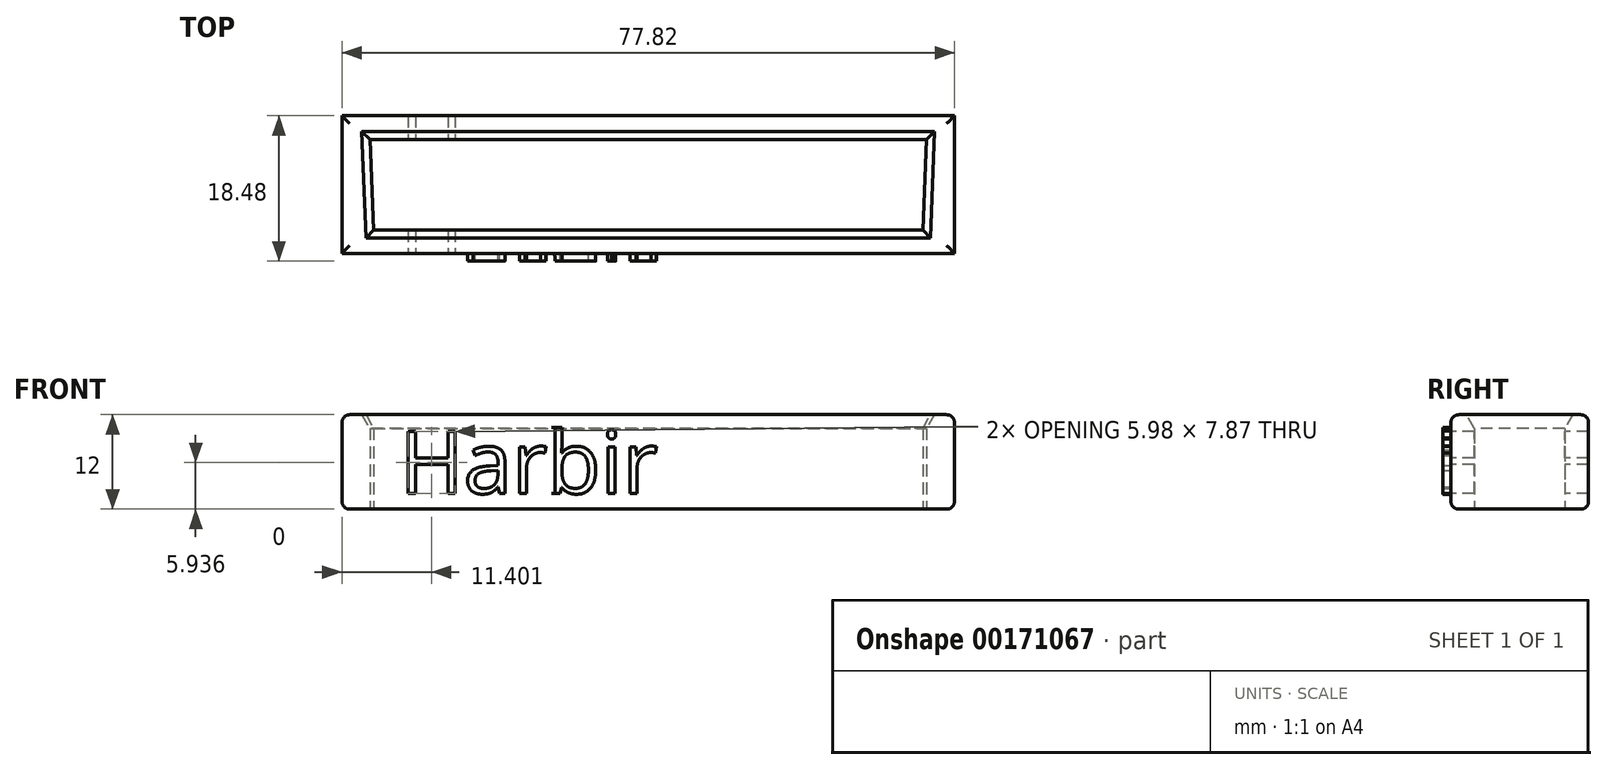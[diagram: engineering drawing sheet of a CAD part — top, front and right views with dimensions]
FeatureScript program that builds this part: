
annotation { "Feature Type Name" : "Feature", "Feature Type Description" : "" }
export const myFeature = defineFeature(function(context is Context, id is Id, definition is map)
    precondition{}
    {
        {
            var Q0;
            Q0=qCreatedBy(makeId("Top.planeOp"),FACE);
            var sketch = newSketch(context, id + "F0", { "sketchPlane" : qUnion([Q0])});
            skLineSegment(sketch, "E0.bottom", {"start": v(-32.53, 27.49) * mm, "end": v(38.17, 27.49) * mm});
            skLineSegment(sketch, "E0.top", {"start": v(-32.53, 16.09) * mm, "end": v(38.17, 16.09) * mm, "construction": true});
            skLineSegment(sketch, "E0.left", {"start": v(-32.53, 27.49) * mm, "end": v(-32.53, 16.09) * mm});
            skLineSegment(sketch, "E0.right", {"start": v(38.17, 27.49) * mm, "end": v(38.17, 16.09) * mm});
            skLineSegment(sketch, "E1", {"start": v(-32.08, 15.99) * mm, "end": v(37.72, 15.99) * mm});
            skLineSegment(sketch, "E2", {"start": v(2.82, 16.09) * mm, "end": v(2.82, 15.99) * mm, "construction": true});
            skLineSegment(sketch, "E3", {"start": v(-32.08, 15.99) * mm, "end": v(-32.53, 27.49) * mm});
            skLineSegment(sketch, "E4", {"start": v(37.72, 15.99) * mm, "end": v(38.17, 27.49) * mm});
            skLineSegment(sketch, "E5.bottom", {"start": v(-36.1, 30.5) * mm, "end": v(41.73, 30.5) * mm});
            skLineSegment(sketch, "E5.top", {"start": v(-36.1, 13.02) * mm, "end": v(41.73, 13.02) * mm});
            skLineSegment(sketch, "E5.left", {"start": v(-36.1, 30.5) * mm, "end": v(-36.1, 13.02) * mm});
            skLineSegment(sketch, "E5.right", {"start": v(41.73, 30.5) * mm, "end": v(41.73, 13.02) * mm});
            skLineSegment(sketch, "E6", {"start": v(2.82, 30.5) * mm, "end": v(2.82, 27.49) * mm, "construction": true});
            skSolve(sketch);
        }
        {
            var Q0;
            Q0=makeQuery(id+"F0.imprint","IMPRINT",FACE,{"disambiguationData":[TD([[makeQuery(id+"F0.imprint","IMPRINT",EDGE,{"derivedFrom":sQuery(id+"F0.wireOp",EDGE,"E0.bottom")}),1.0]])]});
            extrude(context, id + "F1", {"entities" : qUnion([Q0]), "depth" : 12 * mm});
        }
        {
            var Q0;
            Q0=makeQuery(id+"F1.opExtrude","CAP_EDGE",EDGE,{"disambiguationData":[OSD([sQuery(id+"F0.wireOp",EDGE,"E5.top")])],"isStart":false});
            var Q1;
            Q1=makeQuery(id+"F1.opExtrude","CAP_EDGE",EDGE,{"disambiguationData":[OSD([sQuery(id+"F0.wireOp",EDGE,"E5.left")])],"isStart":false});
            var Q2;
            Q2=makeQuery(id+"F1.opExtrude","CAP_EDGE",EDGE,{"disambiguationData":[OSD([sQuery(id+"F0.wireOp",EDGE,"E5.right")])],"isStart":false});
            var Q3;
            Q3=makeQuery(id+"F1.opExtrude","CAP_EDGE",EDGE,{"disambiguationData":[OSD([sQuery(id+"F0.wireOp",EDGE,"E5.bottom")])],"isStart":false});
            var Q4;
            Q4=makeQuery(id+"F1.opExtrude","CAP_EDGE",EDGE,{"disambiguationData":[OSD([sQuery(id+"F0.wireOp",EDGE,"E5.top")])],"isStart":true});
            var Q5;
            Q5=makeQuery(id+"F1.opExtrude","CAP_EDGE",EDGE,{"disambiguationData":[OSD([sQuery(id+"F0.wireOp",EDGE,"E5.right")])],"isStart":true});
            var Q6;
            Q6=makeQuery(id+"F1.opExtrude","CAP_EDGE",EDGE,{"disambiguationData":[OSD([sQuery(id+"F0.wireOp",EDGE,"E5.bottom")])],"isStart":true});
            var Q7;
            Q7=makeQuery(id+"F1.opExtrude","CAP_EDGE",EDGE,{"disambiguationData":[OSD([sQuery(id+"F0.wireOp",EDGE,"E5.left")])],"isStart":true});
            fillet(context, id + "F2", {"entities" : qUnion([Q0, Q1, Q2, Q3, Q4, Q5, Q6, Q7]), "radius" : 1 * mm, "tangentPropagation" : true, "allowEdgeOverflow" : false});
        }
        {
            var Q0;
            Q0=makeQuery(id+"F1.opExtrude","CAP_EDGE",EDGE,{"disambiguationData":[OSD([sQuery(id+"F0.wireOp",EDGE,"E0.bottom")])],"isStart":false});
            var Q1;
            Q1=makeQuery(id+"F1.opExtrude","CAP_EDGE",EDGE,{"disambiguationData":[OSD([sQuery(id+"F0.wireOp",EDGE,"E4")])],"isStart":false});
            var Q2;
            Q2=makeQuery(id+"F1.opExtrude","CAP_EDGE",EDGE,{"disambiguationData":[OSD([sQuery(id+"F0.wireOp",EDGE,"E1")])],"isStart":false});
            var Q3;
            Q3=makeQuery(id+"F1.opExtrude","CAP_EDGE",EDGE,{"disambiguationData":[OSD([sQuery(id+"F0.wireOp",EDGE,"E3")])],"isStart":false});
            chamfer(context, id + "F3", {"entities" : qUnion([Q0, Q1, Q2, Q3]), "chamferType" : ChamferType.OFFSET_ANGLE, "width" : 1 * mm, "oppositeDirection" : false, "angle" : 60 * degree, "tangentPropagation" : true});
        }
        {
            var Q0;
            Q0=makeQuery(id+"F1.opExtrude","SWEPT_FACE",FACE,{"disambiguationData":[OSD([sQuery(id+"F0.wireOp",EDGE,"E5.top")])]});
            var sketch = newSketch(context, id + "F4", { "sketchPlane" : qUnion([Q0])});
            skText(sketch, "E7", { "text": "Harbir", "fontName": "OpenSans-Regular.ttf"});
            const initialGuessF4  = {"E7": [-0.02876, 0.002, 1, 0, 0.00794]};
            skSetInitialGuess(sketch, initialGuessF4);
            skSolve(sketch);
        }
        {
            var Q0;
            Q0=makeQuery(id+"F4.imprint","IMPRINT",FACE,{"disambiguationData":[TD([[makeQuery(id+"F4.imprint","IMPRINT",EDGE,{"derivedFrom":sQuery(id+"F4.wireOp",EDGE,"E7.sketch_text.stroke-12")}),-1.0]])]});
            var Q1;
            Q1=makeQuery(id+"F4.imprint","IMPRINT",FACE,{"disambiguationData":[TD([[makeQuery(id+"F4.imprint","IMPRINT",EDGE,{"derivedFrom":sQuery(id+"F4.wireOp",EDGE,"E7.sketch_text.stroke-39")}),-1.0]])]});
            var Q2;
            Q2=makeQuery(id+"F4.imprint","IMPRINT",FACE,{"disambiguationData":[TD([[makeQuery(id+"F4.imprint","IMPRINT",EDGE,{"derivedFrom":sQuery(id+"F4.wireOp",EDGE,"E7.sketch_text.stroke-52")}),-1.0]])]});
            var Q3;
            Q3=makeQuery(id+"F4.imprint","IMPRINT",FACE,{"disambiguationData":[TD([[makeQuery(id+"F4.imprint","IMPRINT",EDGE,{"derivedFrom":sQuery(id+"F4.wireOp",EDGE,"E7.sketch_text.stroke-79")}),-1.0]])]});
            var Q4;
            Q4=makeQuery(id+"F4.imprint","IMPRINT",FACE,{"disambiguationData":[TD([[makeQuery(id+"F4.imprint","IMPRINT",EDGE,{"derivedFrom":sQuery(id+"F4.wireOp",EDGE,"E7.sketch_text.stroke-75")}),-1.0]])]});
            var Q5;
            Q5=makeQuery(id+"F4.imprint","IMPRINT",FACE,{"disambiguationData":[TD([[makeQuery(id+"F4.imprint","IMPRINT",EDGE,{"derivedFrom":sQuery(id+"F4.wireOp",EDGE,"E7.sketch_text.stroke-87")}),-1.0]])]});
            extrude(context, id + "F5", {"entities" : qUnion([Q0, Q1, Q2, Q3, Q4, Q5]), "operationType" : NewBodyOperationType.ADD, "depth" : 1 * mm});
        }
        {
            var Q0;
            Q0=makeQuery(id+"F4.imprint","IMPRINT",FACE,{"disambiguationData":[TD([[makeQuery(id+"F4.imprint","IMPRINT",EDGE,{"derivedFrom":sQuery(id+"F4.wireOp",EDGE,"E7.sketch_text.stroke-0")}),-1.0]])]});
            var Q1;
            Q1=makeQuery(id+"F1.opExtrude","SWEPT_FACE",FACE,{"disambiguationData":[OSD([sQuery(id+"F0.wireOp",EDGE,"E5.bottom")])]});
            extrude(context, id + "F6", {"entities" : qUnion([Q0]), "operationType" : NewBodyOperationType.REMOVE, "endBound" : BoundingType.UP_TO_SURFACE, "oppositeDirection" : true, "endBoundEntityFace" : qUnion([Q1]), "depth" : 25 * mm});
        }
        {
            var Q0;
            Q0=makeQuery(id+"F5.opExtrude","CAP_EDGE",EDGE,{"disambiguationData":[OSD([sQuery(id+"F4.wireOp",EDGE,"E7.sketch_text.stroke-61")])],"isStart":true});
            fillet(context, id + "F7", {"entities" : qUnion([Q0]), "radius" : 0.4 * mm, "tangentPropagation" : true, "allowEdgeOverflow" : false});
        }
    });
